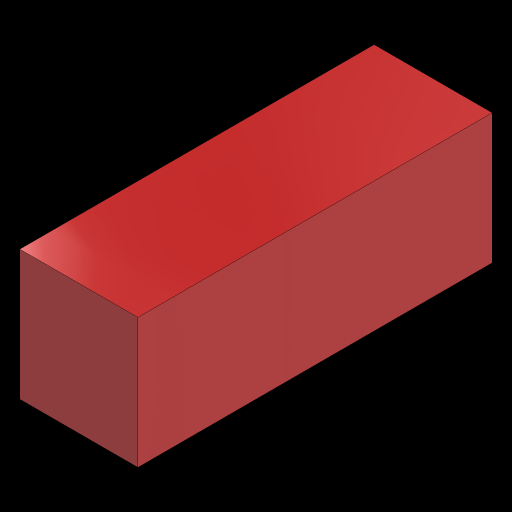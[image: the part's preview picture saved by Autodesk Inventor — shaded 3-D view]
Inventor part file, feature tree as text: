
AUTODESK INVENTOR PART (.ipt)
format: ipt  version: 2023.2 (Build 272271030, 271C)  size: 92,672 bytes
history: native  units: mm
features: extrude x1, sketch x1
ambient origin geometry x8: Origin, YZ Plane, XZ Plane, XY Plane, X Axis, Y Axis, Z Axis, Center Point
bodies: Solid1 (feature_tree)
feature tree (2):
  extrude  "Extrusion1"  Depth=11.0mm
  sketch  "Sketch1"  dims[d0=10.0mm d1=11.0mm d2=30.0mm d3=0.0mm]
